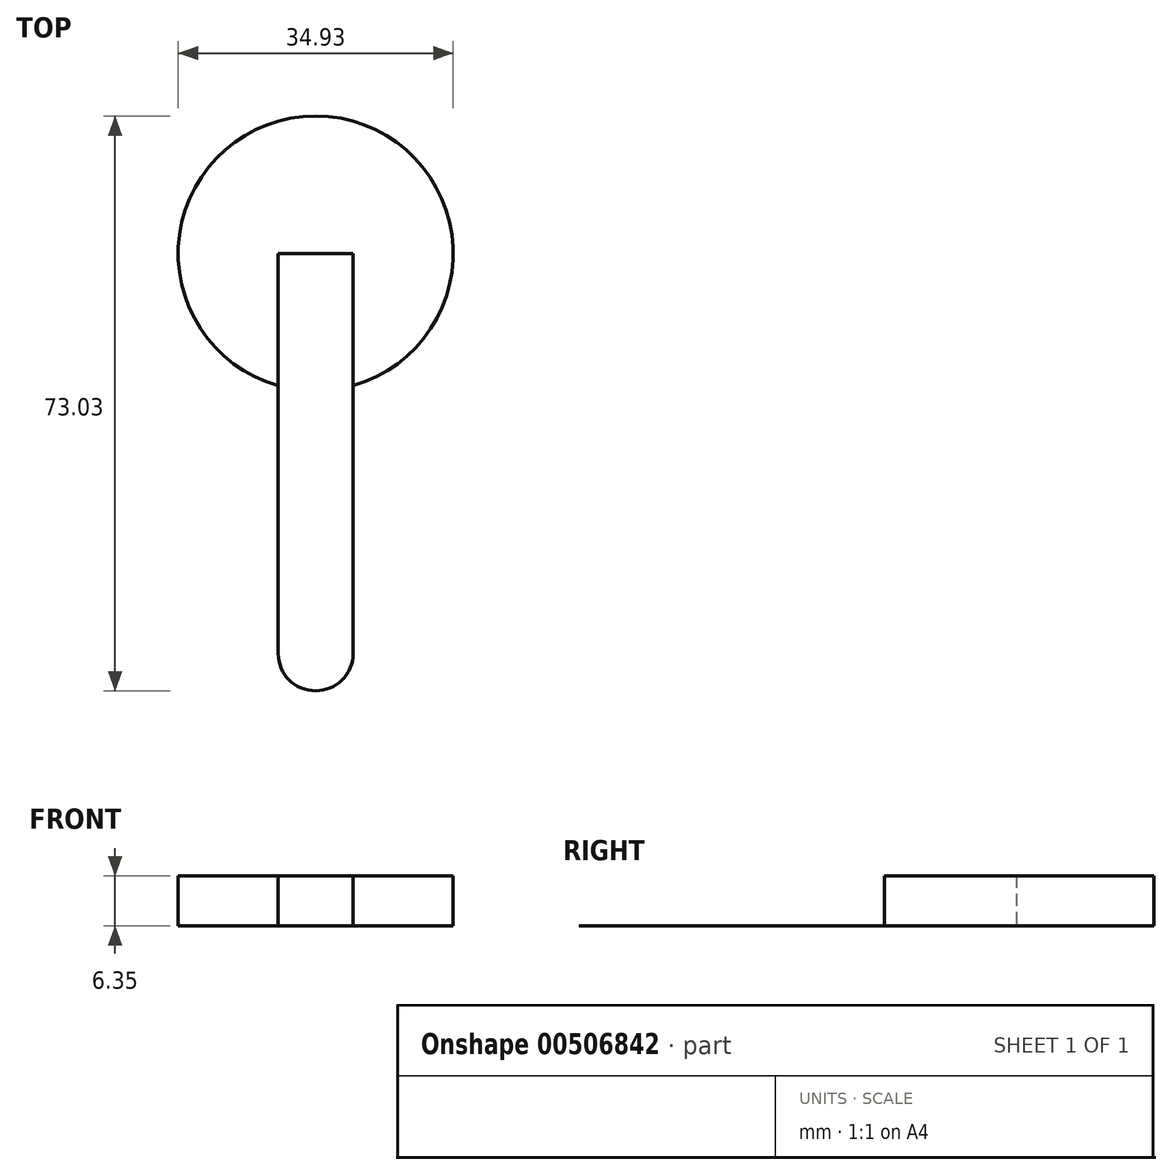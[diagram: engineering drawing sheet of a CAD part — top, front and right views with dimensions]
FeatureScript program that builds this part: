
annotation { "Feature Type Name" : "Feature", "Feature Type Description" : "" }
export const myFeature = defineFeature(function(context is Context, id is Id, definition is map)
    precondition{}
    {
        {
            var Q0;
            Q0=qCreatedBy(makeId("Top.planeOp"),FACE);
            var sketch = newSketch(context, id + "F0", { "sketchPlane" : qUnion([Q0])});
            skCircle(sketch, "E0", {"center": v(-28.77, 6.98) * mm, "radius": 17.46 * mm});
            skPoint(sketch, "E1", {"position": v(-33.53, 6.98) * mm});
            skPoint(sketch, "E2", {"position": v(-24, 6.98) * mm});
            skLineSegment(sketch, "E3", {"start": v(-33.53, 6.98) * mm, "end": v(-33.53, -43.82) * mm});
            skLineSegment(sketch, "E4", {"start": v(-24, 6.98) * mm, "end": v(-24, -43.82) * mm});
            skLineSegment(sketch, "E5", {"start": v(-24, 6.98) * mm, "end": v(-33.53, 6.98) * mm});
            skArc(sketch, "E6", {"start": v(-33.53, -43.82) * mm, "mid": v(-28.77, -48.58) * mm, "end": v(-24, -43.82) * mm});
            skSolve(sketch);
        }
        {
            var Q0;
            {var subQ5=sQuery(id+"F0.wireOp",EDGE,"E5");Q0=makeQuery(id+"F0.imprint","IMPRINT",FACE,{"disambiguationData":[TD([[makeQuery(id+"F0.imprint","IMPRINT",EDGE,{"derivedFrom":subQ5}),-1.0]])]});}
            extrude(context, id + "F1", {"entities" : qUnion([Q0]), "depth" : 6.35 * mm, "offsetDistance" : 25.4 * mm});
        }
        {
            var Q0;
            {var subQ5=sQuery(id+"F0.wireOp",EDGE,"E5");Q0=makeQuery(id+"F0.imprint","IMPRINT",FACE,{"disambiguationData":[TD([[makeQuery(id+"F0.imprint","IMPRINT",EDGE,{"derivedFrom":subQ5}),1.0]])]});}
            var Q1;
            {var subQ5=sQuery(id+"F0.wireOp",EDGE,"E6");Q1=makeQuery(id+"F0.imprint","IMPRINT",FACE,{"disambiguationData":[TD([[makeQuery(id+"F0.imprint","IMPRINT",EDGE,{"derivedFrom":subQ5}),1.0]])]});}
            extrude(context, id + "F2", {"entities" : qUnion([Q0, Q1]), "operationType" : NewBodyOperationType.ADD, "depth" : 5 / 406.4 * mm, "offsetDistance" : 25.4 * mm});
        }
        {
            var Q0;
            {var subQ5=sQuery(id+"F0.wireOp",EDGE,"E6");Q0=makeQuery(id+"F0.imprint","IMPRINT",FACE,{"disambiguationData":[TD([[makeQuery(id+"F0.imprint","IMPRINT",EDGE,{"derivedFrom":subQ5}),1.0]])]});}
            var Q1;
            {var subQ5=sQuery(id+"F0.wireOp",EDGE,"E5");Q1=makeQuery(id+"F0.imprint","IMPRINT",FACE,{"disambiguationData":[TD([[makeQuery(id+"F0.imprint","IMPRINT",EDGE,{"derivedFrom":subQ5}),1.0]])]});}
            extrude(context, id + "F3", {"entities" : qUnion([Q0, Q1]), "operationType" : NewBodyOperationType.ADD, "oppositeDirection" : true, "depth" : 1 / 406.4 * mm, "offsetDistance" : 25.4 * mm});
        }
    });
